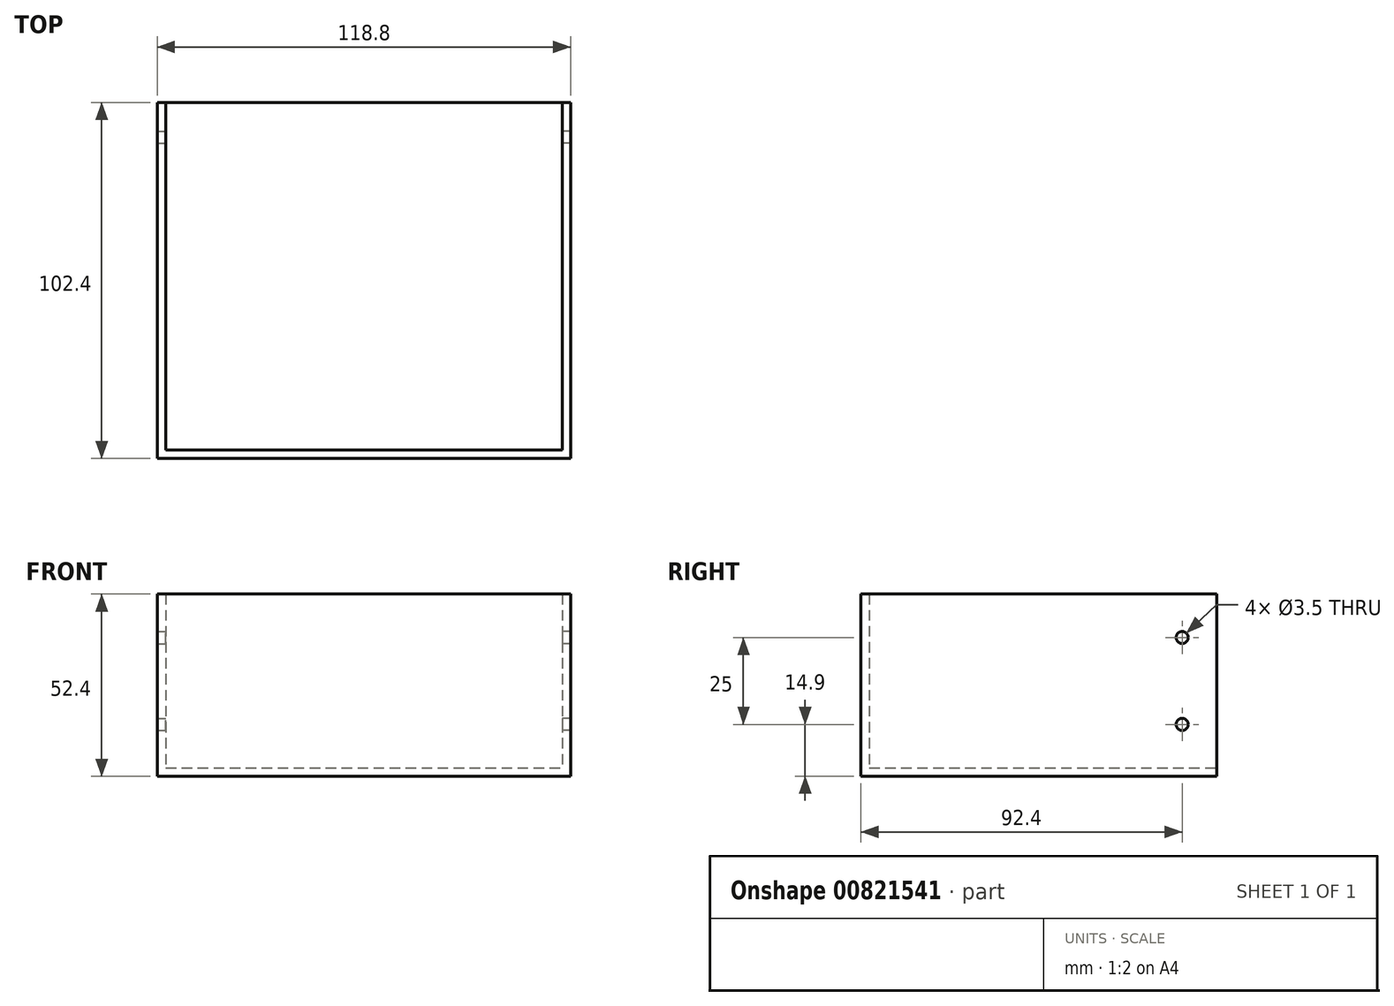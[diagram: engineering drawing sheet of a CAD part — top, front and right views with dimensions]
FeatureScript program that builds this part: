
annotation { "Feature Type Name" : "Feature", "Feature Type Description" : "" }
export const myFeature = defineFeature(function(context is Context, id is Id, definition is map)
    precondition{}
    {
        {
            var Q0;
            Q0=qCreatedBy(makeId("Top.planeOp"),FACE);
            var sketch = newSketch(context, id + "F0", { "sketchPlane" : qUnion([Q0])});
            skLineSegment(sketch, "E0.bottom", {"start": v(-57, 50) * mm, "end": v(57, 50) * mm});
            skLineSegment(sketch, "E0.top", {"start": v(-57, -50) * mm, "end": v(57, -50) * mm});
            skLineSegment(sketch, "E0.left", {"start": v(-57, 50) * mm, "end": v(-57, -50) * mm});
            skLineSegment(sketch, "E0.right", {"start": v(57, 50) * mm, "end": v(57, -50) * mm});
            skPoint(sketch, "E0.middle", {"position": v(0, 0) * mm});
            skLineSegment(sketch, "E1.bottom", {"start": v(-59.4, 50) * mm, "end": v(59.4, 50) * mm});
            skLineSegment(sketch, "E1.top", {"start": v(-59.4, -52.4) * mm, "end": v(59.4, -52.4) * mm});
            skLineSegment(sketch, "E1.left", {"start": v(-59.4, 50) * mm, "end": v(-59.4, -52.4) * mm});
            skLineSegment(sketch, "E1.right", {"start": v(59.4, 50) * mm, "end": v(59.4, -52.4) * mm});
            skSolve(sketch);
        }
        {
            var Q0;
            Q0 = qSketchRegion(id + "F0", true);
            extrude(context, id + "F1", {"entities" : qUnion([Q0]), "depth" : 2.4 * mm, "offsetDistance" : 25 * mm});
        }
        {
            var Q0;
            Q0=makeQuery(id+"F0.imprint","IMPRINT",FACE,{"disambiguationData":[TD([[makeQuery(id+"F0.imprint","IMPRINT",EDGE,{"derivedFrom":sQuery(id+"F0.wireOp",EDGE,"E0.top")}),-1.0]])]});
            extrude(context, id + "F2", {"entities" : qUnion([Q0]), "operationType" : NewBodyOperationType.ADD, "depth" : (50 + 2.4) * mm, "offsetDistance" : 25 * mm});
        }
        {
            var Q0;
            Q0=makeQuery(id+"F2.opExtrude","SWEPT_FACE",FACE,{"disambiguationData":[OSD([sQuery(id+"F0.wireOp",EDGE,"E0.right")])]});
            var sketch = newSketch(context, id + "F3", { "sketchPlane" : qUnion([Q0])});
            skLineSegment(sketch, "E2.0", {"start": v(50, 2.4) * mm, "end": v(-50, 2.4) * mm});
            skLineSegment(sketch, "E2.1", {"start": v(50, 52.4) * mm, "end": v(50, 2.4) * mm});
            skLineSegment(sketch, "E3.0", {"start": v(-50, 52.4) * mm, "end": v(-50, 2.4) * mm});
            skLineSegment(sketch, "E4.0", {"start": v(-50, 52.4) * mm, "end": v(50, 52.4) * mm});
            skCircle(sketch, "E5", {"center": v(-40, 39.9) * mm, "radius": 1.75 * mm});
            skCircle(sketch, "E6", {"center": v(-40, 14.9) * mm, "radius": 1.75 * mm});
            skLineSegment(sketch, "E7", {"start": v(-40, 39.9) * mm, "end": v(-40, 14.9) * mm, "construction": true});
            skPoint(sketch, "E8", {"position": v(-40, 27.4) * mm});
            skSolve(sketch);
        }
        {
            var Q0;
            Q0=makeQuery(id+"F3.imprint","IMPRINT",FACE,{"disambiguationData":[TD([[makeQuery(id+"F3.imprint","IMPRINT",EDGE,{"derivedFrom":sQuery(id+"F3.wireOp",EDGE,"E5")}),1.0]])]});
            var Q1;
            Q1=makeQuery(id+"F3.imprint","IMPRINT",FACE,{"disambiguationData":[TD([[makeQuery(id+"F3.imprint","IMPRINT",EDGE,{"derivedFrom":sQuery(id+"F3.wireOp",EDGE,"E6")}),1.0]])]});
            extrude(context, id + "F4", {"entities" : qUnion([Q0, Q1]), "operationType" : NewBodyOperationType.REMOVE, "endBound" : BoundingType.THROUGH_ALL, "oppositeDirection" : true, "depth" : 25 * mm, "offsetDistance" : 25 * mm});
        }
        {
            var Q0;
            Q0=makeQuery(id+"F3.imprint","IMPRINT",FACE,{"disambiguationData":[TD([[makeQuery(id+"F3.imprint","IMPRINT",EDGE,{"derivedFrom":sQuery(id+"F3.wireOp",EDGE,"E5")}),1.0]])]});
            var Q1;
            Q1=makeQuery(id+"F3.imprint","IMPRINT",FACE,{"disambiguationData":[TD([[makeQuery(id+"F3.imprint","IMPRINT",EDGE,{"derivedFrom":sQuery(id+"F3.wireOp",EDGE,"E6")}),1.0]])]});
            extrude(context, id + "F5", {"entities" : qUnion([Q0, Q1]), "operationType" : NewBodyOperationType.REMOVE, "endBound" : BoundingType.THROUGH_ALL, "depth" : 25 * mm, "offsetDistance" : 25 * mm});
        }
    });
